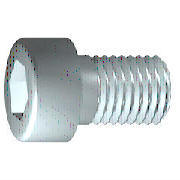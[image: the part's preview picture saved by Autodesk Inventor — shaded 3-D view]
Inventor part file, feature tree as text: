
AUTODESK INVENTOR PART (.ipt)
format: ipt  version: 2021 (Build 250183000, 183)  size: 197,120 bytes
history: native  units: mm (DEFAULTED — no unit token found)
features: sketch x2, extrude x1, plane x1, fillet x1
ambient origin geometry x7: Origin, YZ Plane, XY Plane, X Axis, Y Axis, Z Axis, Center Point
bodies: Solid1 (feature_tree), Body (feature_tree)
feature tree (5):
  extrude  "Slot"  Depth=12.0mm
  plane  "Work Plane1"
  fillet  "Fillet2"  Radius=12.0mm
  sketch  "Sketch1"  dims[d1=20.625mm d2=1.073638mm d3=12.0mm]
  sketch  "Sketch2"  dims[d4=6.0mm d5=60.0deg d6=12.0mm d7=12.0mm d8=11.547005mm d9=18.0mm d10=90.0deg d11=10.0mm d12=0.0mm d13=20.625mm d14=0.0mm d15=1.073538mm d16=1.073538mm d17=1.2mm d19=0.0mm d26=25.0mm d27=45.0deg d28=0.0mm d29=0.0mm d30=0.1mm]
